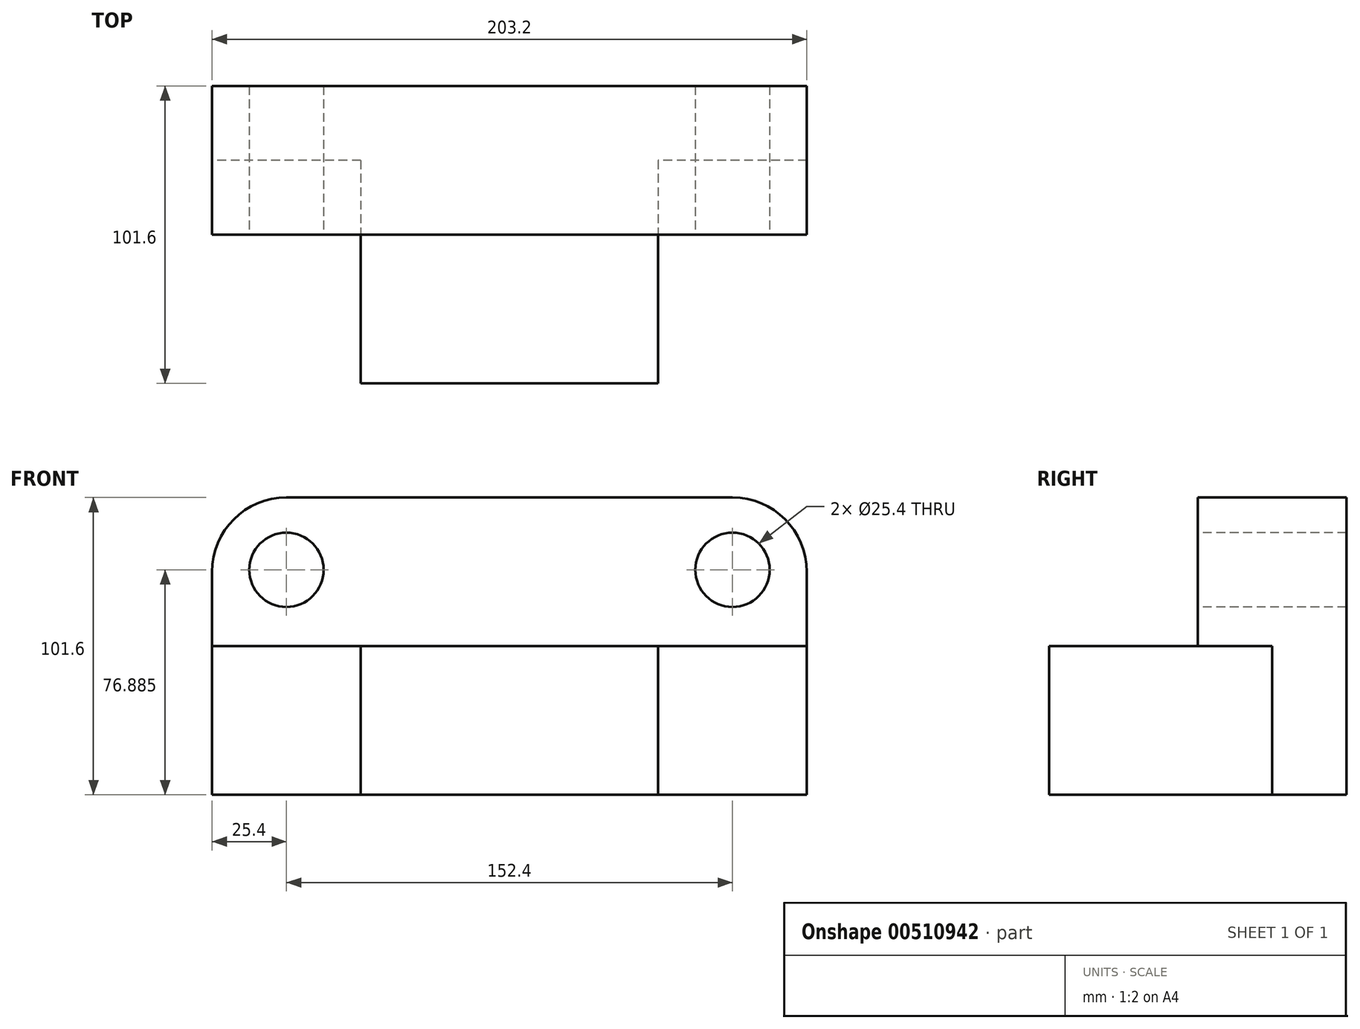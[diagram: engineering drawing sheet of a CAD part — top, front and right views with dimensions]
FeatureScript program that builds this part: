
annotation { "Feature Type Name" : "Feature", "Feature Type Description" : "" }
export const myFeature = defineFeature(function(context is Context, id is Id, definition is map)
    precondition{}
    {
        {
            var Q0;
            Q0=qCreatedBy(makeId("Top.planeOp"),FACE);
            var sketch = newSketch(context, id + "F0", { "sketchPlane" : qUnion([Q0])});
            skLineSegment(sketch, "E0.bottom", {"start": v(0, 0) * mm, "end": v(-203.2, 0) * mm});
            skLineSegment(sketch, "E0.top", {"start": v(0, -101.6) * mm, "end": v(-203.2, -101.6) * mm});
            skLineSegment(sketch, "E0.left", {"start": v(0, 0) * mm, "end": v(0, -101.6) * mm});
            skLineSegment(sketch, "E0.right", {"start": v(-203.2, 0) * mm, "end": v(-203.2, -101.6) * mm});
            skSolve(sketch);
        }
        {
            var Q0;
            Q0 = qSketchRegion(id + "F0", true);
            extrude(context, id + "F1", {"entities" : qUnion([Q0]), "depth" : 101.6 * mm});
        }
        {
            var Q0;
            Q0=makeQuery(id+"F1.opExtrude","CAP_FACE",FACE,{"disambiguationData":[OSD([sQuery(id+"F0.wireOp",EDGE,"E0.bottom"),sQuery(id+"F0.wireOp",EDGE,"E0.top"),sQuery(id+"F0.wireOp",EDGE,"E0.left"),sQuery(id+"F0.wireOp",EDGE,"E0.right")])],"isStart":false});
            var sketch = newSketch(context, id + "F2", { "sketchPlane" : qUnion([Q0])});
            skLineSegment(sketch, "E1.bottom", {"start": v(-203.2, -101.6) * mm, "end": v(0, -101.6) * mm});
            skLineSegment(sketch, "E1.top", {"start": v(-203.2, -50.8) * mm, "end": v(0, -50.8) * mm});
            skLineSegment(sketch, "E1.left", {"start": v(-203.2, -101.6) * mm, "end": v(-203.2, -50.8) * mm});
            skLineSegment(sketch, "E1.right", {"start": v(0, -101.6) * mm, "end": v(0, -50.8) * mm});
            skSolve(sketch);
        }
        {
            var Q0;
            Q0 = qSketchRegion(id + "F2", true);
            extrude(context, id + "F3", {"entities" : qUnion([Q0]), "operationType" : NewBodyOperationType.REMOVE, "oppositeDirection" : true, "depth" : 50.8 * mm});
        }
        {
            var Q0;
            Q0=makeQuery(id+"F1.opExtrude","SWEPT_FACE",FACE,{"disambiguationData":[OSD([sQuery(id+"F0.wireOp",EDGE,"E0.top")])]});
            var sketch = newSketch(context, id + "F4", { "sketchPlane" : qUnion([Q0])});
            skLineSegment(sketch, "E2.bottom", {"start": v(-203.2, 0) * mm, "end": v(-152.4, 0) * mm});
            skLineSegment(sketch, "E2.top", {"start": v(-203.2, 50.8) * mm, "end": v(-152.4, 50.8) * mm});
            skLineSegment(sketch, "E2.left", {"start": v(-203.2, 0) * mm, "end": v(-203.2, 50.8) * mm});
            skLineSegment(sketch, "E2.right", {"start": v(-152.4, 0) * mm, "end": v(-152.4, 50.8) * mm});
            skSolve(sketch);
        }
        {
            var Q0;
            Q0 = qSketchRegion(id + "F4", true);
            extrude(context, id + "F5", {"entities" : qUnion([Q0]), "operationType" : NewBodyOperationType.REMOVE, "oppositeDirection" : true, "depth" : 76.2 * mm});
        }
        {
            var Q0;
            Q0=makeQuery(id+"F1.opExtrude","SWEPT_FACE",FACE,{"disambiguationData":[OSD([sQuery(id+"F0.wireOp",EDGE,"E0.top")])]});
            var sketch = newSketch(context, id + "F6", { "sketchPlane" : qUnion([Q0])});
            skLineSegment(sketch, "E3.bottom", {"start": v(0, 0) * mm, "end": v(-50.8, 0) * mm});
            skLineSegment(sketch, "E3.top", {"start": v(0, 50.8) * mm, "end": v(-50.8, 50.8) * mm});
            skLineSegment(sketch, "E3.left", {"start": v(0, 0) * mm, "end": v(0, 50.8) * mm});
            skLineSegment(sketch, "E3.right", {"start": v(-50.8, 0) * mm, "end": v(-50.8, 50.8) * mm});
            skSolve(sketch);
        }
        {
            var Q0;
            Q0 = qSketchRegion(id + "F6", true);
            extrude(context, id + "F7", {"entities" : qUnion([Q0]), "operationType" : NewBodyOperationType.REMOVE, "oppositeDirection" : true, "depth" : 76.2 * mm});
        }
        {
            var Q0;
            Q0=makeQuery(id+"F3.boolean.opBoolean","COPY",FACE,{"derivedFrom":makeQuery(id+"F3.opExtrude","SWEPT_FACE",FACE,{"disambiguationData":[OSD([sQuery(id+"F2.wireOp",EDGE,"E1.top")])]})});
            var sketch = newSketch(context, id + "F8", { "sketchPlane" : qUnion([Q0])});
            skCircle(sketch, "E4", {"center": v(-177.8, 76.89) * mm, "radius": 12.7 * mm});
            skCircle(sketch, "E5", {"center": v(-25.4, 76.89) * mm, "radius": 12.7 * mm});
            skSolve(sketch);
        }
        {
            var Q0;
            Q0 = qSketchRegion(id + "F8", true);
            extrude(context, id + "F9", {"entities" : qUnion([Q0]), "operationType" : NewBodyOperationType.REMOVE, "oppositeDirection" : true, "depth" : 50.8 * mm});
        }
        {
            var Q0;
            Q0=makeQuery(id+"F1.opExtrude","CAP_EDGE",EDGE,{"disambiguationData":[OSD([sQuery(id+"F0.wireOp",EDGE,"E0.right")])],"isStart":false});
            var Q1;
            Q1=makeQuery(id+"F1.opExtrude","CAP_EDGE",EDGE,{"disambiguationData":[OSD([sQuery(id+"F0.wireOp",EDGE,"E0.left")])],"isStart":false});
            fillet(context, id + "F10", {"entities" : qUnion([Q0, Q1]), "radius" : 25.4 * mm, "tangentPropagation" : true, "allowEdgeOverflow" : false});
        }
    });
